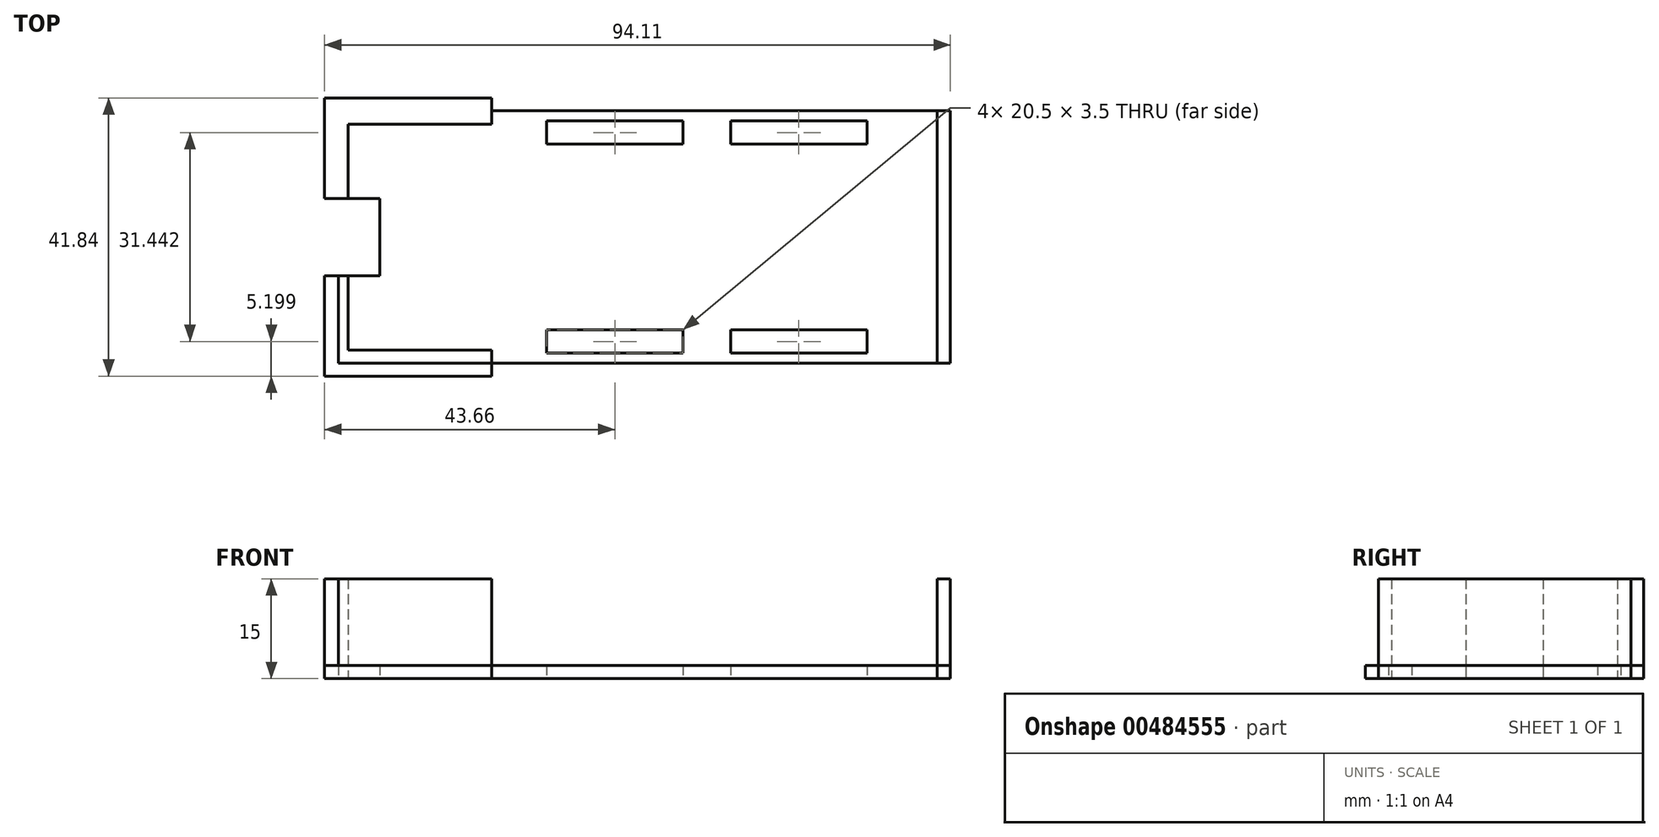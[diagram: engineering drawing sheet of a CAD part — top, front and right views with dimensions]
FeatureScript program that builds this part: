
annotation { "Feature Type Name" : "Feature", "Feature Type Description" : "" }
export const myFeature = defineFeature(function(context is Context, id is Id, definition is map)
    precondition{}
    {
        {
            var Q0;
            Q0=qCreatedBy(makeId("Top.planeOp"),FACE);
            var sketch = newSketch(context, id + "F0", { "sketchPlane" : qUnion([Q0])});
            skLineSegment(sketch, "E0.bottom", {"start": v(-46, 19) * mm, "end": v(46, 19) * mm});
            skLineSegment(sketch, "E0.top", {"start": v(-46, -19) * mm, "end": v(46, -19) * mm});
            skLineSegment(sketch, "E0.left", {"start": v(-46, 19) * mm, "end": v(-46, 5.82) * mm});
            skLineSegment(sketch, "E0.right", {"start": v(46, 19) * mm, "end": v(46, -19) * mm});
            skPoint(sketch, "E0.middle", {"position": v(0, 0) * mm});
            skLineSegment(sketch, "E1.bottom", {"start": v(-14.7, -17.47) * mm, "end": v(5.8, -17.47) * mm});
            skLineSegment(sketch, "E1.top", {"start": v(-14.7, -13.97) * mm, "end": v(5.8, -13.97) * mm});
            skLineSegment(sketch, "E1.left", {"start": v(-14.7, -17.47) * mm, "end": v(-14.7, -13.97) * mm});
            skLineSegment(sketch, "E1.right", {"start": v(5.8, -17.47) * mm, "end": v(5.8, -13.97) * mm});
            skLineSegment(sketch, "E2.bottom", {"start": v(12.96, -17.47) * mm, "end": v(33.46, -17.47) * mm});
            skLineSegment(sketch, "E2.top", {"start": v(12.96, -13.97) * mm, "end": v(33.46, -13.97) * mm});
            skLineSegment(sketch, "E2.left", {"start": v(12.96, -17.47) * mm, "end": v(12.96, -13.97) * mm});
            skLineSegment(sketch, "E2.right", {"start": v(33.46, -17.47) * mm, "end": v(33.46, -13.97) * mm});
            skLineSegment(sketch, "E3", {"start": v(-46, -17) * mm, "end": v(-23, -17) * mm});
            skLineSegment(sketch, "E4", {"start": v(-23, -17) * mm, "end": v(-23, -19) * mm});
            skLineSegment(sketch, "E5", {"start": v(-23, -20.92) * mm, "end": v(-46, -20.92) * mm});
            skLineSegment(sketch, "E6", {"start": v(-46, -20.92) * mm, "end": v(-23, -20.92) * mm});
            skLineSegment(sketch, "E7", {"start": v(-23, -19) * mm, "end": v(-23, -20.92) * mm});
            skLineSegment(sketch, "E8", {"start": v(-44.6, -17) * mm, "end": v(-44.6, -5.82) * mm});
            skLineSegment(sketch, "E9", {"start": v(-44.6, -5.82) * mm, "end": v(-46, -5.82) * mm});
            skLineSegment(sketch, "E10", {"start": v(-46, -5.82) * mm, "end": v(-48.1, -5.82) * mm});
            skLineSegment(sketch, "E11", {"start": v(-48.1, -5.82) * mm, "end": v(-48.1, -20.92) * mm});
            skLineSegment(sketch, "E12", {"start": v(-48.1, -20.92) * mm, "end": v(-46, -20.92) * mm});
            skLineSegment(sketch, "E13", {"start": v(44, 19) * mm, "end": v(44, -19) * mm});
            skLineSegment(sketch, "E14.MirrorCS", {"start": v(-44.6, 17) * mm, "end": v(-44.6, 5.82) * mm});
            skLineSegment(sketch, "E15.MirrorCS", {"start": v(-44.6, 5.82) * mm, "end": v(-46, 5.82) * mm});
            skLineSegment(sketch, "E16.MirrorCS", {"start": v(-46, 5.82) * mm, "end": v(-48.1, 5.82) * mm});
            skLineSegment(sketch, "E17.MirrorCS", {"start": v(-48.1, 5.82) * mm, "end": v(-48.1, 20.92) * mm});
            skLineSegment(sketch, "E18.MirrorCS", {"start": v(-46, 20.92) * mm, "end": v(-23, 20.92) * mm});
            skLineSegment(sketch, "E19.MirrorCS", {"start": v(-48.1, 20.92) * mm, "end": v(-46, 20.92) * mm});
            skLineSegment(sketch, "E20.MirrorCS", {"start": v(-23, 19) * mm, "end": v(-23, 20.92) * mm});
            skLineSegment(sketch, "E21.MirrorCS", {"start": v(-23, 17) * mm, "end": v(-23, 19) * mm});
            skLineSegment(sketch, "E22.MirrorCS", {"start": v(-46, 17) * mm, "end": v(-23, 17) * mm});
            skLineSegment(sketch, "E23.MirrorCS", {"start": v(-14.7, 17.47) * mm, "end": v(5.8, 17.47) * mm});
            skLineSegment(sketch, "E24.MirrorCS", {"start": v(-14.7, 17.47) * mm, "end": v(-14.7, 13.97) * mm});
            skLineSegment(sketch, "E25.MirrorCS", {"start": v(-14.7, 13.97) * mm, "end": v(5.8, 13.97) * mm});
            skLineSegment(sketch, "E26.MirrorCS", {"start": v(5.8, 17.47) * mm, "end": v(5.8, 13.97) * mm});
            skLineSegment(sketch, "E27.MirrorCS", {"start": v(12.96, 17.47) * mm, "end": v(33.46, 17.47) * mm});
            skLineSegment(sketch, "E28.MirrorCS", {"start": v(12.96, 17.47) * mm, "end": v(12.96, 13.97) * mm});
            skLineSegment(sketch, "E29.MirrorCS", {"start": v(12.96, 13.97) * mm, "end": v(33.46, 13.97) * mm});
            skLineSegment(sketch, "E30.MirrorCS", {"start": v(33.46, 17.47) * mm, "end": v(33.46, 13.97) * mm});
            skLineSegment(sketch, "E31", {"start": v(-44.6, -5.82) * mm, "end": v(-39.8, -5.82) * mm});
            skLineSegment(sketch, "E32", {"start": v(-39.8, -5.82) * mm, "end": v(-39.8, 5.82) * mm});
            skLineSegment(sketch, "E33", {"start": v(-39.8, 5.82) * mm, "end": v(-44.6, 5.82) * mm});
            skLineSegment(sketch, "E34.trimOffspring", {"start": v(-46, -5.82) * mm, "end": v(-46, -19) * mm});
            skSolve(sketch);
        }
        {
            var Q0;
            {var subQ0=sQuery(id+"F0.wireOp",EDGE,"E0.right");Q0=makeQuery(id+"F0.imprint","IMPRINT",FACE,{"disambiguationData":[TD([[makeQuery(id+"F0.imprint","IMPRINT",EDGE,{"derivedFrom":subQ0}),-1.0]])]});}
            var Q1;
            {var subQ0=sQuery(id+"F0.wireOp",EDGE,"E16.MirrorCS");Q1=makeQuery(id+"F0.imprint","IMPRINT",FACE,{"disambiguationData":[TD([[makeQuery(id+"F0.imprint","IMPRINT",EDGE,{"derivedFrom":subQ0}),-1.0]])]});}
            var Q2;
            Q2=makeQuery(id+"F0.imprint","IMPRINT",FACE,{"disambiguationData":[TD([[makeQuery(id+"F0.imprint","IMPRINT",EDGE,{"derivedFrom":sQuery(id+"F0.wireOp",EDGE,"E6")}),1.0]])]});
            var Q3;
            {var subQ6=sQuery(id+"F0.wireOp",EDGE,"E21.MirrorCS");Q3=makeQuery(id+"F0.imprint","IMPRINT",FACE,{"disambiguationData":[TD([[makeQuery(id+"F0.imprint","IMPRINT",EDGE,{"derivedFrom":subQ6}),1.0]])]});}
            var Q4;
            {var subQ0=sQuery(id+"F0.wireOp",EDGE,"E4");Q4=makeQuery(id+"F0.imprint","IMPRINT",FACE,{"disambiguationData":[TD([[makeQuery(id+"F0.imprint","IMPRINT",EDGE,{"derivedFrom":subQ0}),-1.0]])]});}
            var Q5;
            {var subQ4=sQuery(id+"F0.wireOp",EDGE,"E14.MirrorCS");Q5=makeQuery(id+"F0.imprint","IMPRINT",FACE,{"disambiguationData":[TD([[makeQuery(id+"F0.imprint","IMPRINT",EDGE,{"derivedFrom":subQ4}),-1.0]])]});}
            var Q6;
            {var subQ4=sQuery(id+"F0.wireOp",EDGE,"E8");Q6=makeQuery(id+"F0.imprint","IMPRINT",FACE,{"disambiguationData":[TD([[makeQuery(id+"F0.imprint","IMPRINT",EDGE,{"derivedFrom":subQ4}),1.0]])]});}
            extrude(context, id + "F1", {"entities" : qUnion([Q0, Q1, Q2, Q3, Q4, Q5, Q6]), "depth" : 15 * mm});
        }
        {
            var Q0;
            Q0 = qSketchRegion(id + "F0", true);
            extrude(context, id + "F2", {"entities" : qUnion([Q0]), "depth" : 2 * mm});
        }
    });
